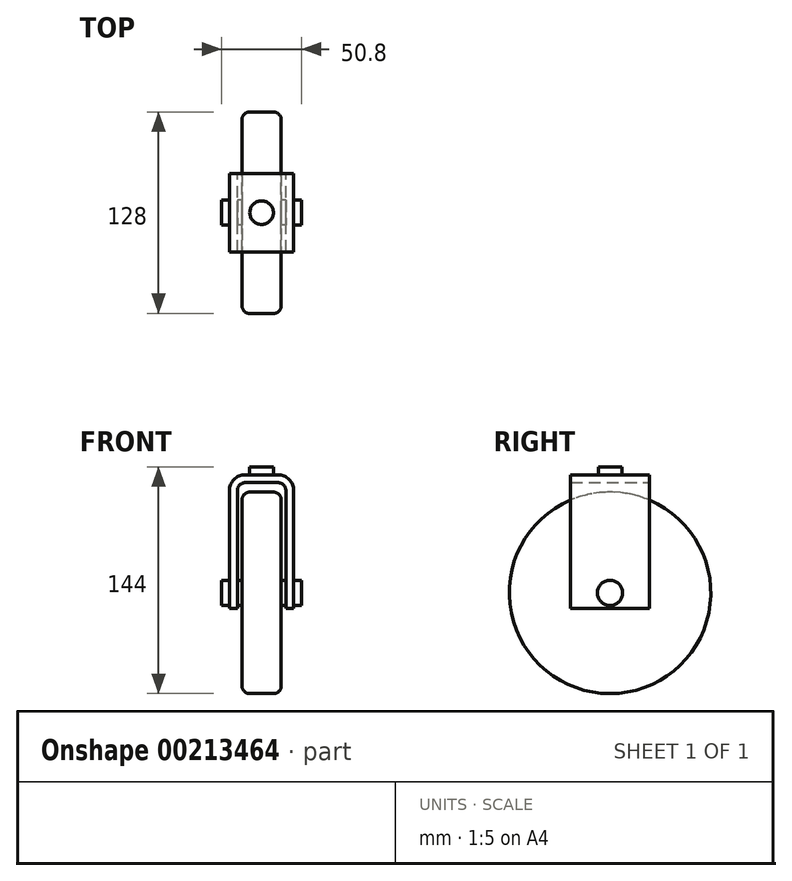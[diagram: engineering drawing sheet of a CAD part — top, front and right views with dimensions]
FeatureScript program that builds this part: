
annotation { "Feature Type Name" : "Feature", "Feature Type Description" : "" }
export const myFeature = defineFeature(function(context is Context, id is Id, definition is map)
    precondition{}
    {
        {
            var Q0;
            Q0=qCreatedBy(makeId("Front.planeOp"),FACE);
            var sketch = newSketch(context, id + "F0", { "sketchPlane" : qUnion([Q0])});
            skLineSegment(sketch, "E0", {"start": v(-87.22, 0) * mm, "end": v(73.7, 0) * mm, "construction": true});
            skLineSegment(sketch, "E1.bottom", {"start": v(-25.4, 8) * mm, "end": v(-20.4, 8) * mm});
            skLineSegment(sketch, "E1.top", {"start": v(-25.4, 0) * mm, "end": v(25.4, 0) * mm});
            skLineSegment(sketch, "E1.left", {"start": v(-25.4, 8) * mm, "end": v(-25.4, 0) * mm});
            skLineSegment(sketch, "E1.right", {"start": v(25.4, 8) * mm, "end": v(25.4, 0) * mm});
            skLineSegment(sketch, "E2.bottom", {"start": v(-7.5, 64) * mm, "end": v(7.5, 64) * mm});
            skLineSegment(sketch, "E2.top", {"start": v(-12.5, 0) * mm, "end": v(12.5, 0) * mm});
            skLineSegment(sketch, "E2.left", {"start": v(-12.5, 59) * mm, "end": v(-12.5, 8) * mm});
            skLineSegment(sketch, "E2.right", {"start": v(12.5, 59) * mm, "end": v(12.5, 8) * mm});
            skLineSegment(sketch, "E3", {"start": v(0, 0) * mm, "end": v(0, 77.8) * mm, "construction": true});
            skPoint(sketch, "E3.endSnap0", {"position": v(0, 64) * mm});
            skPoint(sketch, "E4.visualSharp", {"position": v(-12.5, 64) * mm});
            skArc(sketch, "E4.filletArc", {"start": v(-7.5, 64) * mm, "mid": v(-11.04, 62.54) * mm, "end": v(-12.5, 59) * mm});
            skPoint(sketch, "E5.visualSharp", {"position": v(12.5, 64) * mm});
            skArc(sketch, "E5.filletArc", {"start": v(12.5, 59) * mm, "mid": v(11.04, 62.54) * mm, "end": v(7.5, 64) * mm});
            skLineSegment(sketch, "E6.0", {"start": v(-15.4, 8) * mm, "end": v(-15.4, 5) * mm});
            skLineSegment(sketch, "E7.0", {"start": v(15.4, 8) * mm, "end": v(15.4, 5) * mm});
            skLineSegment(sketch, "E8.0", {"start": v(-20.4, 8) * mm, "end": v(-20.4, 5) * mm});
            skLineSegment(sketch, "E9.0", {"start": v(20.4, 8) * mm, "end": v(20.4, 5) * mm});
            skLineSegment(sketch, "E10.0", {"start": v(-20.4, 5) * mm, "end": v(-15.4, 5) * mm});
            skLineSegment(sketch, "E11.trimOffspring", {"start": v(15.4, 5) * mm, "end": v(20.4, 5) * mm});
            skLineSegment(sketch, "E12.trimOffspring", {"start": v(20.4, 8) * mm, "end": v(25.4, 8) * mm});
            skLineSegment(sketch, "E13.trimOffspring", {"start": v(-15.4, 8) * mm, "end": v(-12.5, 8) * mm});
            skLineSegment(sketch, "E14.trimOffspring", {"start": v(12.5, 8) * mm, "end": v(15.4, 8) * mm});
            skSolve(sketch);
        }
        {
            var Q0;
            Q0=makeQuery(id+"F0.imprint","IMPRINT",FACE,{"disambiguationData":[TD([[makeQuery(id+"F0.imprint","IMPRINT",EDGE,{"derivedFrom":sQuery(id+"F0.wireOp",EDGE,"E1.bottom")}),-1.0]])]});
            var Q1;
            Q1=sQuery(id+"F0.wireOp",EDGE,"E0");
            revolve(context, id + "F1", {"entities" : qUnion([Q0]), "axis" : qUnion([Q1]), "revolveType" : RevolveType.FULL});
        }
        {
            var Q0;
            Q0=qCreatedBy(makeId("Front.planeOp"),FACE);
            var sketch = newSketch(context, id + "F2", { "sketchPlane" : qUnion([Q0])});
            skLineSegment(sketch, "E15", {"start": v(-15.4, -10) * mm, "end": v(-20.4, -10) * mm});
            skLineSegment(sketch, "E16", {"start": v(-20.4, -10) * mm, "end": v(-20.4, 65) * mm});
            skLineSegment(sketch, "E17", {"start": v(-10.4, 75) * mm, "end": v(0, 75) * mm});
            skLineSegment(sketch, "E18", {"start": v(-15.4, -10) * mm, "end": v(-15.4, 65) * mm});
            skLineSegment(sketch, "E19.0", {"start": v(-10.4, 70) * mm, "end": v(0, 70) * mm});
            skArc(sketch, "E20.filletArc", {"start": v(-10.4, 70) * mm, "mid": v(-13.94, 68.54) * mm, "end": v(-15.4, 65) * mm});
            skArc(sketch, "E21.0", {"start": v(-10.4, 75) * mm, "mid": v(-17.47, 72.07) * mm, "end": v(-20.4, 65) * mm});
            skLineSegment(sketch, "E22", {"start": v(0, 82.5) * mm, "end": v(0, -89.77) * mm, "construction": true});
            skArc(sketch, "E23.MirrorCS", {"start": v(10.4, 70) * mm, "mid": v(13.94, 68.54) * mm, "end": v(15.4, 65) * mm});
            skLineSegment(sketch, "E24.MirrorCS", {"start": v(15.4, -10) * mm, "end": v(20.4, -10) * mm});
            skArc(sketch, "E25.MirrorCS", {"start": v(10.4, 75) * mm, "mid": v(17.47, 72.07) * mm, "end": v(20.4, 65) * mm});
            skLineSegment(sketch, "E26.MirrorCS", {"start": v(15.4, -10) * mm, "end": v(15.4, 65) * mm});
            skLineSegment(sketch, "E27.MirrorCS", {"start": v(10.4, 75) * mm, "end": v(0, 75) * mm});
            skLineSegment(sketch, "E28.MirrorCS", {"start": v(10.4, 70) * mm, "end": v(0, 70) * mm});
            skLineSegment(sketch, "E29.MirrorCS", {"start": v(20.4, -10) * mm, "end": v(20.4, 65) * mm});
            skSolve(sketch);
        }
        {
            var Q0;
            Q0=makeQuery(id+"F2.imprint","IMPRINT",FACE,{"disambiguationData":[TD([[makeQuery(id+"F2.imprint","IMPRINT",EDGE,{"derivedFrom":sQuery(id+"F2.wireOp",EDGE,"E15")}),-1.0]])]});
            extrude(context, id + "F3", {"entities" : qUnion([Q0]), "operationType" : NewBodyOperationType.ADD, "endBound" : BoundingType.SYMMETRIC, "depth" : 50 * mm});
        }
        {
            var Q0;
            Q0=makeQuery(id+"F3.opExtrude","SWEPT_FACE",FACE,{"disambiguationData":[OSD([sQuery(id+"F2.wireOp",EDGE,"E17"),sQuery(id+"F2.wireOp",EDGE,"E27.MirrorCS")])]});
            var sketch = newSketch(context, id + "F4", { "sketchPlane" : qUnion([Q0])});
            skCircle(sketch, "E30", {"center": v(0, 0) * mm, "radius": 7.5 * mm});
            skSolve(sketch);
        }
        {
            var Q0;
            Q0=qSketchRegion(id+"F4",true);
            extrude(context, id + "F5", {"entities" : qUnion([Q0]), "operationType" : NewBodyOperationType.ADD, "depth" : 5 * mm});
        }
    });
